# Revit family: 346477xx0--Vitreous china wall - hung WC- horizontal outlet - The Gap - Roca - 346477xx0
name_source: partatom
category: Plumbing Fixtures
units: mm (PartAtom-declared; Revit-internal decimal feet)

## family parameters
Always vertical = Yes
Cut with Voids When Loaded = No
Host = Wall
OmniClass Number = 23.45.00.00
OmniClass Title = Sanitary, Laundry, and Cleaning Equipment
Part Type = Normal
Room Calculation Point = No
Round Connector Dimension = Use Diameter
Shared = No

## types (2) — shared parameters
BIMobject category = WC
Date of publishing = 2015-03-06
Depth = 350
Description = Vitreous china wall-hung WC with horizontal outlet
Design country = Spain
Eco green certification = No
Edition number = 2
Flush water connection = 55 mm  [stored 0.180446 ft]
Flushing system = Washdown
Height = 400 mm  [stored 1.31234 ft]
IFC Classification = Sanitary Terminal
Installation type = Wall-hung
Length = 350 mm
Manufacturer country = Spain
Manufacturer name = Roca
Manufacturer url = http://www.roca.com
Material main = Vitreous china
Model = 346477xx0
NBS Reference Code = 35-65-90
NBS Reference Description = Toilet Systems
Nominal height = 400.00
Nominal width = 540.00
Outlet type = Horizontal
Product SKU = 346477xx0
Product data url = http://roca.bimobject.com
Product family = The Gap
Product group = Toilets
QR code = https://www.roca.com
Shape = Square
Suitable for Children = No
Suitable for Handicapped = No
Technical description = http://www.roca.com
UNSPSC Code = 301815
URL = http://www.roca.com
Uniclass 1.4 Code = L7216
Uniclass 1.4 Description = Toilets
Uniclass 2.0 Code = SS-35-65-90
Uniclass 2.0 Description = Toilet Systems
Waste Water Connection = 102 mm
Weight Net (Kg) = 25
Width = 540 mm  [stored 1.77165 ft]

## per-type parameters (varying)
| type | Ref. No. |
| Pergamon - The Gap - Roca | 346477170 |
| White - The Gap - Roca | 346477000 |

note: column(s) folded — value = type name in every type: Material

note: [stored X ft] marks values corroborated as IEEE doubles in the binary element streams (Revit-internal decimal feet)

## geometry (parser evidence)
native form markers: Blend x2, Sweep x1
no freeform markers — native parametric forms only
